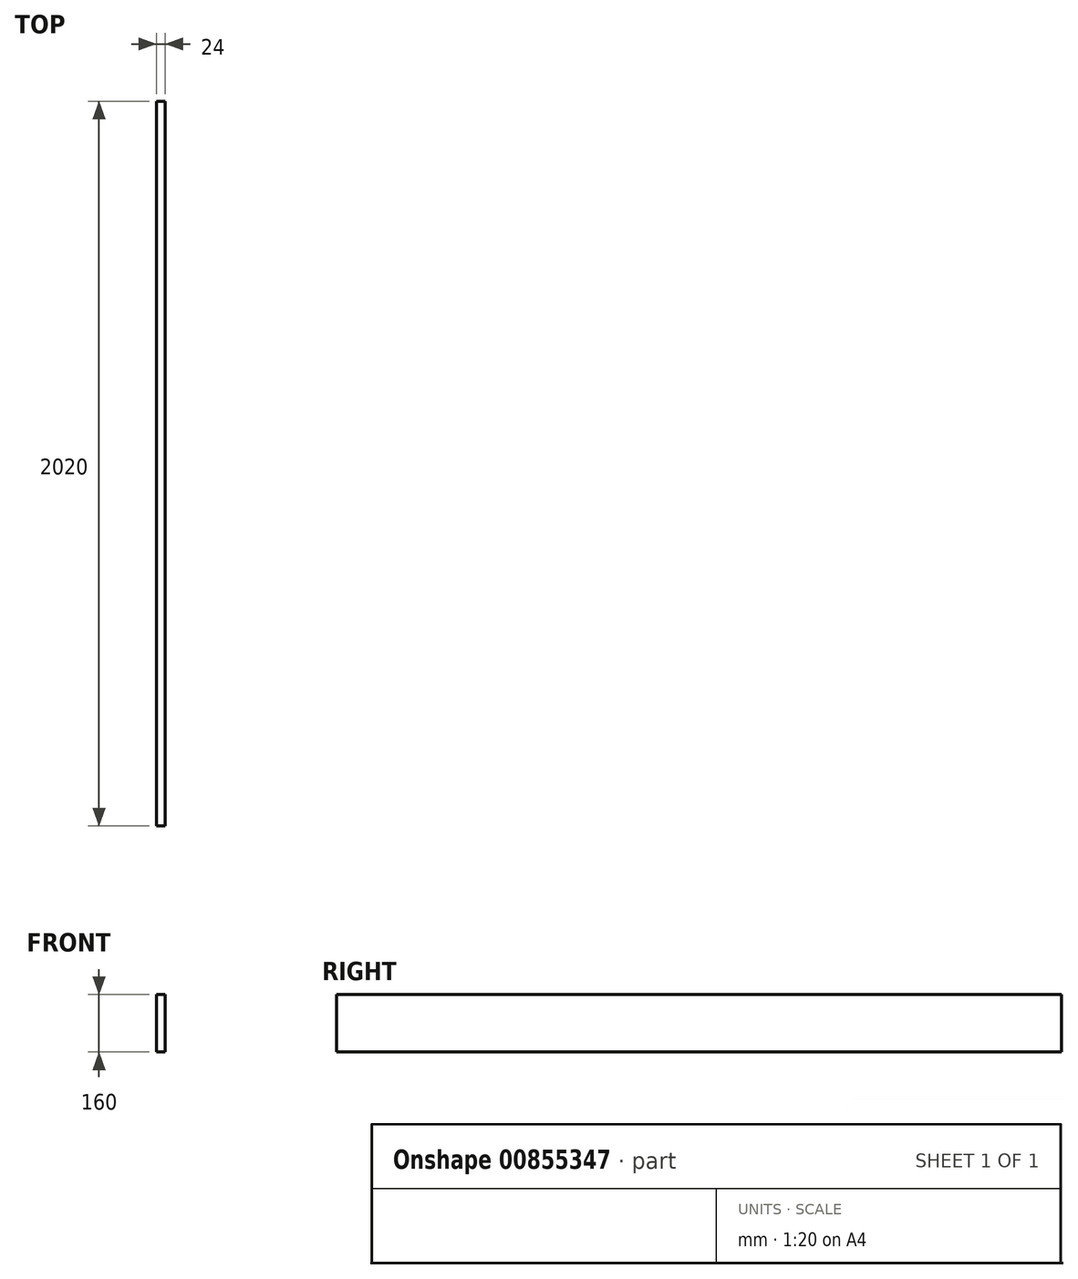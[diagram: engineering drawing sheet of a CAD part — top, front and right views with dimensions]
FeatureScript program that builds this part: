
annotation { "Feature Type Name" : "Feature", "Feature Type Description" : "" }
export const myFeature = defineFeature(function(context is Context, id is Id, definition is map)
    precondition{}
    {
        {
            var Q0;
            Q0=qCreatedBy(makeId("Right.planeOp"),FACE);
            var sketch = newSketch(context, id + "F0", { "sketchPlane" : qUnion([Q0])});
            skLineSegment(sketch, "E0.bottom", {"start": v(0, 0) * mm, "end": v(2020, 0) * mm});
            skLineSegment(sketch, "E0.top", {"start": v(0, 160) * mm, "end": v(2020, 160) * mm});
            skLineSegment(sketch, "E0.left", {"start": v(0, 0) * mm, "end": v(0, 160) * mm});
            skLineSegment(sketch, "E0.right", {"start": v(2020, 0) * mm, "end": v(2020, 160) * mm});
            skSolve(sketch);
        }
        {
            var Q0;
            Q0 = qSketchRegion(id + "F0", true);
            extrude(context, id + "F1", {"entities" : qUnion([Q0]), "depth" : 24 * mm, "offsetDistance" : 25 * mm});
        }
    });
